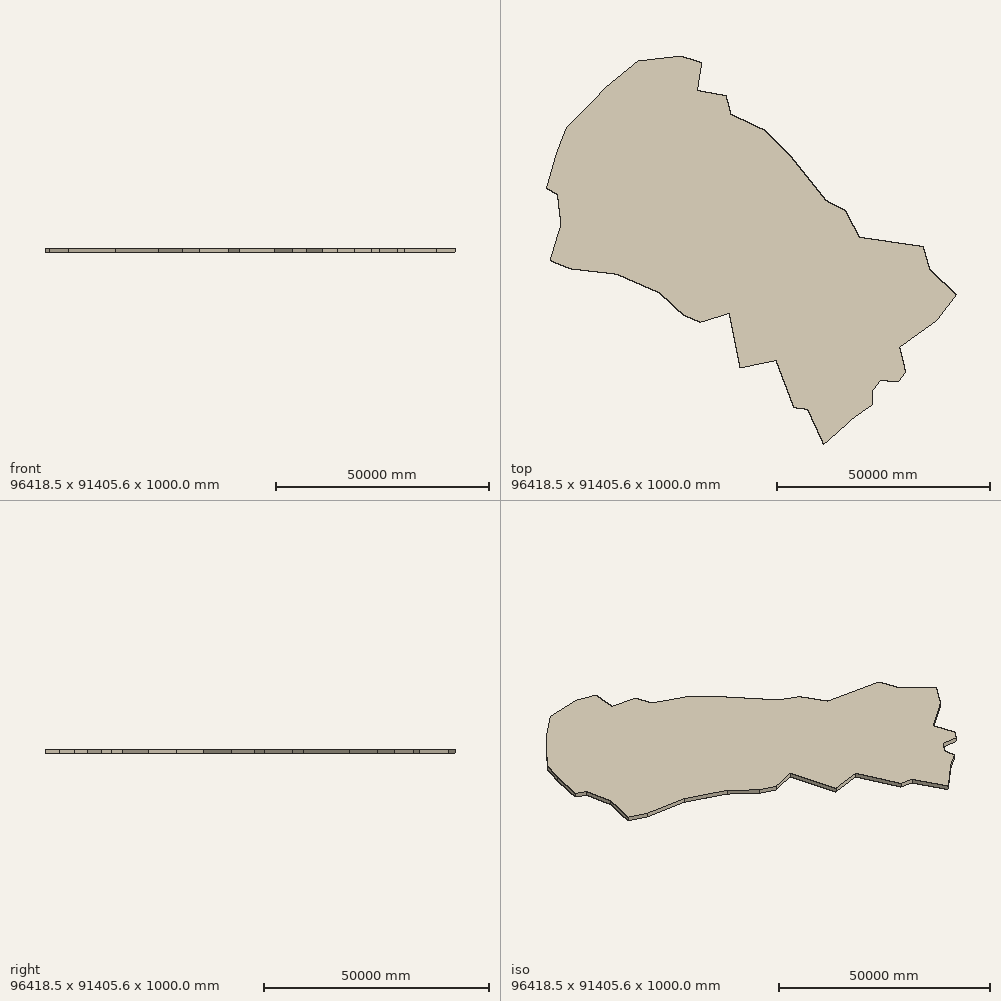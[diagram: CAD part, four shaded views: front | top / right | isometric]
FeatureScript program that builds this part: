
annotation { "Feature Type Name" : "Feature", "Feature Type Description" : "" }
export const myFeature = defineFeature(function(context is Context, id is Id, definition is map)
    precondition{}
    {
        {
            var Q0;
            Q0=qCreatedBy(makeId("Top.planeOp"),FACE);
            var sketch = newSketch(context, id + "F0", { "sketchPlane" : qUnion([Q0])});
            skLineSegment(sketch, "E0", {"start": v(-2665.36, -27633.34) * mm, "end": v(5781.44, -25877.27) * mm});
            skLineSegment(sketch, "E1", {"start": v(5781.44, -25877.27) * mm, "end": v(9992.36, -36926.36) * mm});
            skLineSegment(sketch, "E2", {"start": v(9992.36, -36926.36) * mm, "end": v(13211.74, -37353.17) * mm});
            skLineSegment(sketch, "E3", {"start": v(13211.74, -37353.17) * mm, "end": v(17042.45, -45687.23) * mm});
            skLineSegment(sketch, "E4", {"start": v(17042.45, -45687.23) * mm, "end": v(20532.17, -42633.8) * mm});
            skLineSegment(sketch, "E5", {"start": v(20532.17, -42633.8) * mm, "end": v(24401.26, -39146.02) * mm});
            skLineSegment(sketch, "E6", {"start": v(24401.26, -39146.02) * mm, "end": v(28546.25, -36301.1) * mm});
            skLineSegment(sketch, "E7", {"start": v(28546.25, -36301.1) * mm, "end": v(28364.28, -33266.03) * mm});
            skLineSegment(sketch, "E8", {"start": v(28364.28, -33266.03) * mm, "end": v(30458.75, -30532.76) * mm});
            skLineSegment(sketch, "E9", {"start": v(30458.75, -30532.76) * mm, "end": v(34628.24, -30887.3) * mm});
            skLineSegment(sketch, "E10", {"start": v(34628.24, -30887.3) * mm, "end": v(36315.06, -28623.65) * mm});
            skLineSegment(sketch, "E11", {"start": v(36315.06, -28623.65) * mm, "end": v(34879.24, -22806.5) * mm});
            skLineSegment(sketch, "E12", {"start": v(34879.24, -22806.5) * mm, "end": v(43658.47, -16501.74) * mm});
            skLineSegment(sketch, "E13", {"start": v(43658.47, -16501.74) * mm, "end": v(48238.17, -10495.3) * mm});
            skLineSegment(sketch, "E14", {"start": v(48238.17, -10495.3) * mm, "end": v(41896.7, -4299.18) * mm});
            skLineSegment(sketch, "E15", {"start": v(41896.7, -4299.18) * mm, "end": v(40420.56, 957.26) * mm});
            skLineSegment(sketch, "E16", {"start": v(40420.56, 957.26) * mm, "end": v(25415.1, 3113.8) * mm});
            skLineSegment(sketch, "E17", {"start": v(25415.1, 3113.8) * mm, "end": v(22125.05, 9386.6) * mm});
            skLineSegment(sketch, "E18", {"start": v(22125.05, 9386.6) * mm, "end": v(17553.84, 11778.85) * mm});
            skLineSegment(sketch, "E19", {"start": v(17553.84, 11778.85) * mm, "end": v(9235.5, 22184.03) * mm});
            skLineSegment(sketch, "E20", {"start": v(9235.5, 22184.03) * mm, "end": v(3285.4, 28221.35) * mm});
            skLineSegment(sketch, "E21", {"start": v(3285.4, 28221.35) * mm, "end": v(-4783.58, 32044.41) * mm});
            skLineSegment(sketch, "E22", {"start": v(-4783.58, 32044.41) * mm, "end": v(-5963.76, 36437.83) * mm});
            skLineSegment(sketch, "E23", {"start": v(-5963.76, 36437.83) * mm, "end": v(-12672.41, 37635.88) * mm});
            skLineSegment(sketch, "E24", {"start": v(-12672.41, 37635.88) * mm, "end": v(-11649.13, 44152.26) * mm});
            skLineSegment(sketch, "E25", {"start": v(-11649.13, 44152.26) * mm, "end": v(-16508.79, 45718.32) * mm});
            skLineSegment(sketch, "E26", {"start": v(-16508.79, 45718.32) * mm, "end": v(-26578.88, 44585.28) * mm});
            skLineSegment(sketch, "E27", {"start": v(-26578.88, 44585.28) * mm, "end": v(-33843.46, 38618.08) * mm});
            skLineSegment(sketch, "E28", {"start": v(-33843.46, 38618.08) * mm, "end": v(-43537.5, 28685.86) * mm});
            skLineSegment(sketch, "E29", {"start": v(-43537.5, 28685.86) * mm, "end": v(-45830.09, 22828.14) * mm});
            skLineSegment(sketch, "E30", {"start": v(-45830.09, 22828.14) * mm, "end": v(-48180.37, 14570.47) * mm});
            skLineSegment(sketch, "E31", {"start": v(-48180.37, 14570.47) * mm, "end": v(-45627.6, 13227.03) * mm});
            skLineSegment(sketch, "E32", {"start": v(-45627.6, 13227.03) * mm, "end": v(-44781.55, 6020.35) * mm});
            skLineSegment(sketch, "E33", {"start": v(-44781.55, 6020.35) * mm, "end": v(-47334.46, -2360.8) * mm});
            skLineSegment(sketch, "E34", {"start": v(-47334.46, -2360.8) * mm, "end": v(-42657.85, -4287.59) * mm});
            skLineSegment(sketch, "E35", {"start": v(-42657.85, -4287.59) * mm, "end": v(-31610.81, -5573.88) * mm});
            skLineSegment(sketch, "E36", {"start": v(-31610.81, -5573.88) * mm, "end": v(-21622.07, -9957.8) * mm});
            skLineSegment(sketch, "E37", {"start": v(-21622.07, -9957.8) * mm, "end": v(-15992.56, -15168.81) * mm});
            skLineSegment(sketch, "E38", {"start": v(-15992.56, -15168.81) * mm, "end": v(-11978.48, -16906.56) * mm});
            skLineSegment(sketch, "E39", {"start": v(-11978.48, -16906.56) * mm, "end": v(-5199.45, -14816.27) * mm});
            skLineSegment(sketch, "E40", {"start": v(-5199.45, -14816.27) * mm, "end": v(-2665.36, -27633.34) * mm});
            skPoint(sketch, "E41", {"position": v(-31126.07, 19630.24) * mm});
            skSolve(sketch);
        }
        {
            var Q0;
            Q0=makeQuery(id+"F0.imprint","IMPRINT",FACE,{"disambiguationData":[TD([[makeQuery(id+"F0.imprint","IMPRINT",EDGE,{"derivedFrom":sQuery(id+"F0.wireOp",EDGE,"E0")}),1.0]])]});
            extrude(context, id + "F1", {"entities" : qUnion([Q0]), "depth" : 1000 * mm, "offsetDistance" : 25 * mm});
        }
    });
